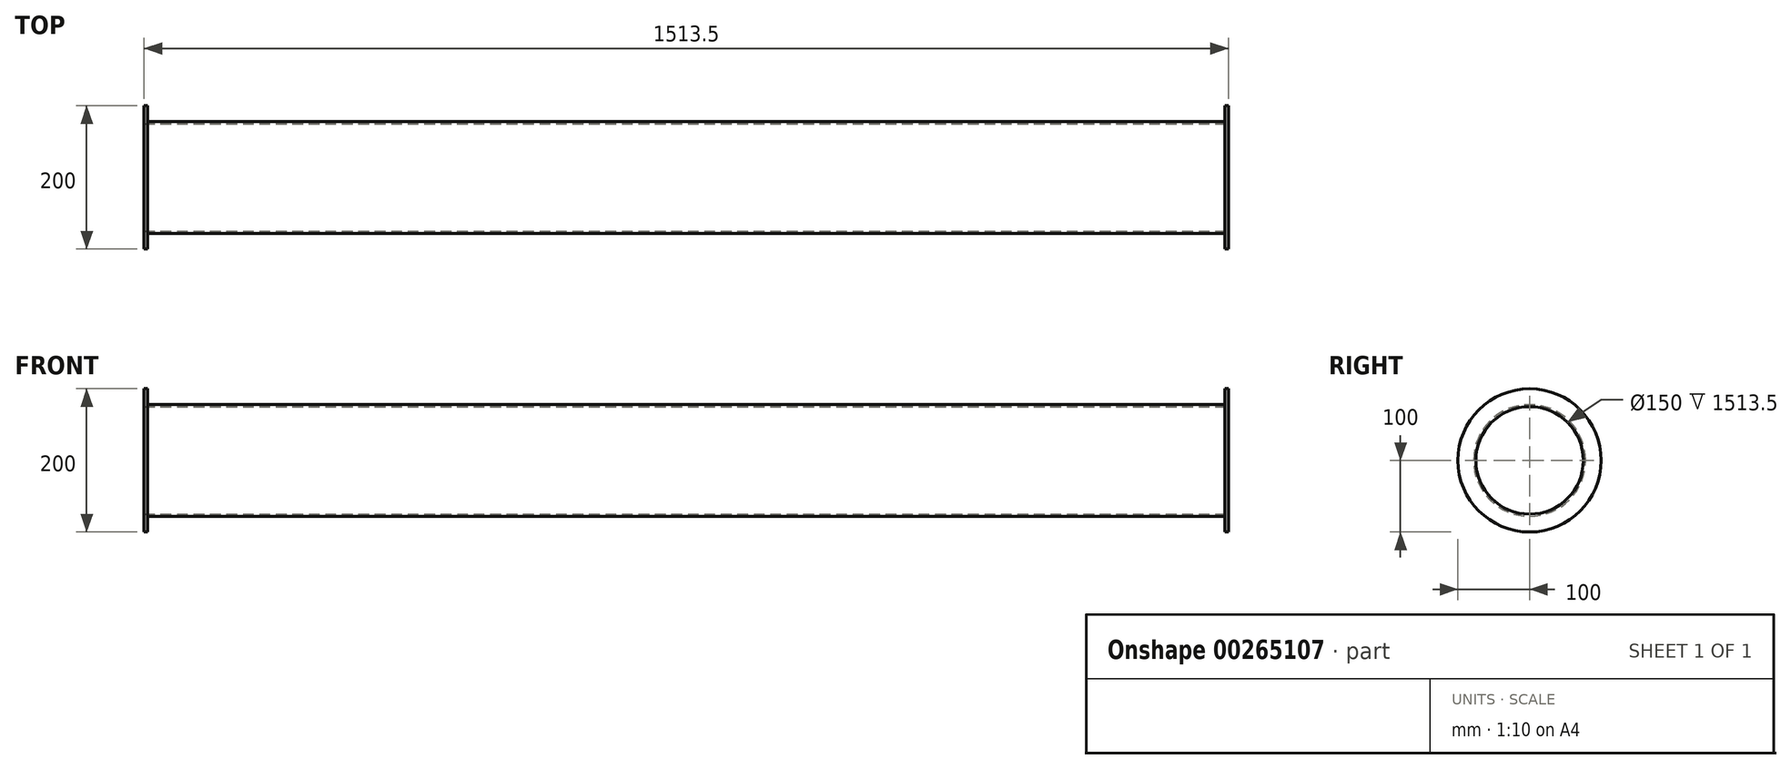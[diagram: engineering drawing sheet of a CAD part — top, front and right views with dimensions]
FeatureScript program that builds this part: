
annotation { "Feature Type Name" : "Feature", "Feature Type Description" : "" }
export const myFeature = defineFeature(function(context is Context, id is Id, definition is map)
    precondition{}
    {
        {
            var Q0;
            Q0=qCreatedBy(makeId("Front.planeOp"),FACE);
            var sketch = newSketch(context, id + "F0", { "sketchPlane" : qUnion([Q0])});
            skLineSegment(sketch, "E0", {"start": v(0, 0) * mm, "end": v(-1503.5, 0) * mm, "construction": true});
            skLineSegment(sketch, "E1.bottom", {"start": v(0, 78) * mm, "end": v(-1503.5, 78) * mm});
            skLineSegment(sketch, "E1.top", {"start": v(0, 75) * mm, "end": v(-1503.5, 75) * mm});
            skLineSegment(sketch, "E1.left", {"start": v(0, 78) * mm, "end": v(0, 75) * mm});
            skLineSegment(sketch, "E1.right", {"start": v(-1503.5, 78) * mm, "end": v(-1503.5, 75) * mm});
            skSolve(sketch);
        }
        {
            var Q0;
            Q0=makeQuery(id+"F0.imprint","IMPRINT",FACE,{"disambiguationData":[TD([[makeQuery(id+"F0.imprint","IMPRINT",EDGE,{"derivedFrom":sQuery(id+"F0.wireOp",EDGE,"E1.bottom")}),1.0]])]});
            var Q1;
            Q1=sQuery(id+"F0.wireOp",EDGE,"E0");
            revolve(context, id + "F1", {"entities" : qUnion([Q0]), "axis" : qUnion([Q1]), "revolveType" : RevolveType.FULL});
        }
        {
            var Q0;
            Q0=makeQuery(id+"F1.opRevolve","SWEPT_FACE",FACE,{"disambiguationData":[OSD([sQuery(id+"F0.wireOp",EDGE,"E1.right")])]});
            var sketch = newSketch(context, id + "F2", { "sketchPlane" : qUnion([Q0])});
            skCircle(sketch, "E2", {"center": v(0, 0) * mm, "radius": 100 * mm});
            skCircle(sketch, "E3", {"center": v(0, 0) * mm, "radius": 75 * mm});
            skSolve(sketch);
        }
        {
            var Q0;
            Q0=makeQuery(id+"F2.imprint","IMPRINT",FACE,{"disambiguationData":[TD([[makeQuery(id+"F2.imprint","IMPRINT",EDGE,{"derivedFrom":sQuery(id+"F2.wireOp",EDGE,"E2")}),1.0]])]});
            var Q1;
            Q1=makeQuery(id+"F2.imprint","IMPRINT",FACE,{"disambiguationData":[TD([[makeQuery(id+"F2.imprint","IMPRINT",EDGE,{"derivedFrom":sQuery(id+"F2.wireOp",EDGE,"E3")}),1.0]])]});
            extrude(context, id + "F3", {"entities" : qUnion([Q0, Q1]), "operationType" : NewBodyOperationType.ADD, "depth" : 5 * mm});
        }
        {
            var Q0;
            Q0=makeQuery(id+"F1.opRevolve","SWEPT_FACE",FACE,{"disambiguationData":[OSD([sQuery(id+"F0.wireOp",EDGE,"E1.left")])]});
            var sketch = newSketch(context, id + "F4", { "sketchPlane" : qUnion([Q0])});
            skCircle(sketch, "E4", {"center": v(0, 0) * mm, "radius": 100 * mm});
            skCircle(sketch, "E5", {"center": v(0, 0) * mm, "radius": 75 * mm});
            skSolve(sketch);
        }
        {
            var Q0;
            Q0=makeQuery(id+"F4.imprint","IMPRINT",FACE,{"disambiguationData":[TD([[makeQuery(id+"F4.imprint","IMPRINT",EDGE,{"derivedFrom":sQuery(id+"F4.wireOp",EDGE,"E4")}),1.0]])]});
            var Q1;
            Q1=makeQuery(id+"F4.imprint","IMPRINT",FACE,{"disambiguationData":[TD([[makeQuery(id+"F4.imprint","IMPRINT",EDGE,{"derivedFrom":sQuery(id+"F4.wireOp",EDGE,"E5")}),-1.0]])]});
            extrude(context, id + "F5", {"entities" : qUnion([Q0, Q1]), "operationType" : NewBodyOperationType.ADD, "depth" : 5 * mm});
        }
    });
